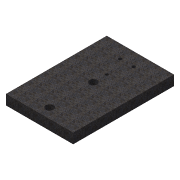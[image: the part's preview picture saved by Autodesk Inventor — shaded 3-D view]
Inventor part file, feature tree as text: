
AUTODESK INVENTOR PART (.ipt)
format: ipt  version: 2016 SP2 (Build 200236200, 236)  size: 126,976 bytes
history: native  units: in
note: dims shown in document units (in); Inventor stores cm internally (conversion verified against a paired STEP export)
features: sketch x5, extrude x3, hole x2
ambient origin geometry x8: Origin, YZ Plane, XZ Plane, XY Plane, X Axis, Y Axis, Z Axis, Center Point
bodies: Solid1 (feature_tree)
feature tree (10):
  extrude  "base"  Depth=59.0551in
  extrude  "air"  Depth=5.9055in
  extrude  "power"  Depth=1.9291in
  hole  "fibre"  [1 undecoded]
  hole  "air2"  [1 undecoded]
  sketch  "Sketch1"  dims[d0=39.3701in d1=59.0551in]
  sketch  "Sketch2"  dims[d2=5.9055in d3=0.0in d4=4.5276in]
  sketch  "Sketch3"  dims[d5=1.0in d6=0.0in d7=1.9291in]
  sketch  "Sketch4"  dims[d9=10.0in d10=0.0in]
  sketch  "Sketch6"  dims[d13=1.7717in d14=0.75in d15=0.375in d16=0.25in d17=0.5635in d18=1.0in d19=0.8108in d29=6.0in d30=25.5906in d31=4.5276in d32=0.75in d33=0.375in d34=0.25in d35=0.5635in d36=1.0in d37=0.8108in d38=27.5591in d40=3.937in d41=1.9291in d42=3.937in d52=1.9291in d53=19.685in d55=7.874in]
note: 2 required parameter values undecoded (feature->parameter linkage not recoverable at this tier; creation-order binding heuristic only, values carry confidence <= 0.55)
